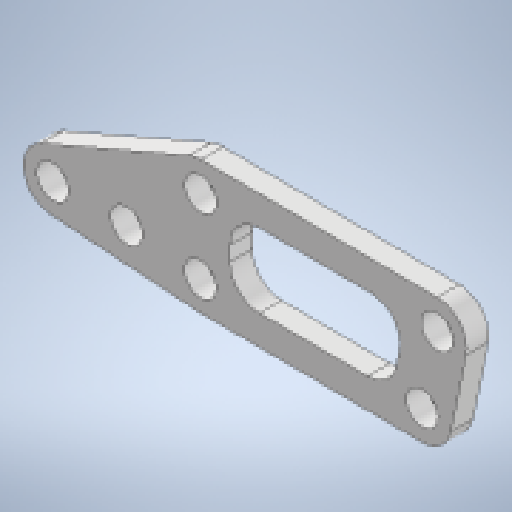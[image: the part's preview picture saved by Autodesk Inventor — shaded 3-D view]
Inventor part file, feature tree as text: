
AUTODESK INVENTOR PART (.ipt)
format: ipt  version: 2025.1 (Build 291241000, 241)  size: 188,416 bytes
history: native  units: mm
features: reference x7, other x5, extrude x1, fillet x1, sketch x1
ambient origin geometry x8: Origin, YZ Plane, XZ Plane, XY Plane, X Axis, Y Axis, Z Axis, Center Point
bodies: Body1 (feature_tree)
feature tree (15):
  other  "ソリッド1"
  extrude  "押し出し1"  Depth=2.2mm
  fillet  "フィレット1"  Radius=2.2mm
  sketch  "スケッチ1"
  reference  "参照1"
  reference  "参照2"
  reference  "参照3"
  reference  "参照4"
  reference  "参照5"
  reference  "参照6"
  reference  "参照7"
  other  "<userpath>\Documents\Inventor\Vixen\doutai.iam"
  other  "doutai.iam"
  other  "ude:1"
  other  "ude_sensor:2"
